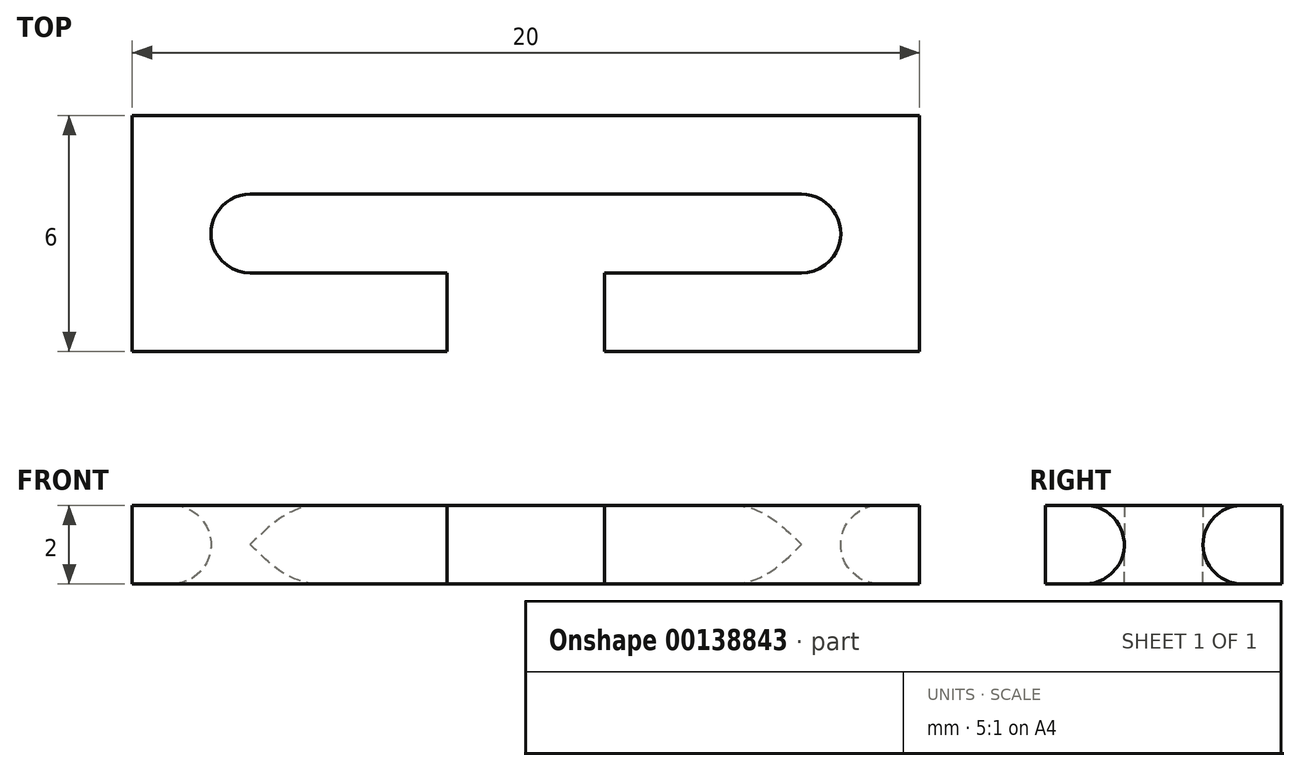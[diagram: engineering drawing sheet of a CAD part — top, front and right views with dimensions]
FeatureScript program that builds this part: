
annotation { "Feature Type Name" : "Feature", "Feature Type Description" : "" }
export const myFeature = defineFeature(function(context is Context, id is Id, definition is map)
    precondition{}
    {
        {
            var Q0;
            Q0=qCreatedBy(makeId("Top.planeOp"),FACE);
            var sketch = newSketch(context, id + "F0", { "sketchPlane" : qUnion([Q0])});
            skLineSegment(sketch, "E0.bottom", {"start": v(-2.27, -2.19) * mm, "end": v(17.73, -2.19) * mm});
            skLineSegment(sketch, "E0.top", {"start": v(-2.27, 3.81) * mm, "end": v(17.73, 3.81) * mm});
            skLineSegment(sketch, "E0.left", {"start": v(-2.27, -2.19) * mm, "end": v(-2.27, 3.81) * mm});
            skLineSegment(sketch, "E0.right", {"start": v(17.73, -2.19) * mm, "end": v(17.73, 3.81) * mm});
            skSolve(sketch);
        }
        {
            var Q0;
            Q0=makeQuery(id+"F0.imprint","IMPRINT",FACE,{"disambiguationData":[TD([[makeQuery(id+"F0.imprint","IMPRINT",EDGE,{"derivedFrom":sQuery(id+"F0.wireOp",EDGE,"E0.bottom")}),1.0]])]});
            extrude(context, id + "F1", {"entities" : qUnion([Q0]), "depth" : 2 * mm});
        }
        {
            var Q0;
            Q0=makeQuery(id+"F1.opExtrude","CAP_FACE",FACE,{"disambiguationData":[OSD([sQuery(id+"F0.wireOp",EDGE,"E0.bottom"),sQuery(id+"F0.wireOp",EDGE,"E0.top"),sQuery(id+"F0.wireOp",EDGE,"E0.left"),sQuery(id+"F0.wireOp",EDGE,"E0.right")])],"isStart":false});
            var Q1;
            Q1=makeQuery(id+"F1.opExtrude","CAP_FACE",FACE,{"disambiguationData":[OSD([sQuery(id+"F0.wireOp",EDGE,"E0.bottom"),sQuery(id+"F0.wireOp",EDGE,"E0.top"),sQuery(id+"F0.wireOp",EDGE,"E0.left"),sQuery(id+"F0.wireOp",EDGE,"E0.right")])],"isStart":true});
            shell(context, id + "F2", {"entities" : qUnion([Q0, Q1]), "thickness" : 2 * mm});
        }
        {
            var Q0;
            Q0=makeQuery(id+"F1.opExtrude","CAP_FACE",FACE,{"disambiguationData":[OSD([sQuery(id+"F0.wireOp",EDGE,"E0.bottom"),sQuery(id+"F0.wireOp",EDGE,"E0.top"),sQuery(id+"F0.wireOp",EDGE,"E0.left"),sQuery(id+"F0.wireOp",EDGE,"E0.right")])],"isStart":false});
            var sketch = newSketch(context, id + "F3", { "sketchPlane" : qUnion([Q0])});
            skLineSegment(sketch, "E1.bottom", {"start": v(5.73, -0.19) * mm, "end": v(9.73, -0.19) * mm});
            skLineSegment(sketch, "E1.top", {"start": v(5.73, -2.19) * mm, "end": v(9.73, -2.19) * mm});
            skLineSegment(sketch, "E1.left", {"start": v(5.73, -0.19) * mm, "end": v(5.73, -2.19) * mm});
            skLineSegment(sketch, "E1.right", {"start": v(9.73, -0.19) * mm, "end": v(9.73, -2.19) * mm});
            skSolve(sketch);
        }
        {
            var Q0;
            Q0=makeQuery(id+"F3.imprint","IMPRINT",FACE,{"disambiguationData":[TD([[makeQuery(id+"F3.imprint","IMPRINT",EDGE,{"derivedFrom":sQuery(id+"F3.wireOp",EDGE,"E1.bottom")}),-1.0]])]});
            extrude(context, id + "F4", {"entities" : qUnion([Q0]), "operationType" : NewBodyOperationType.REMOVE, "oppositeDirection" : true, "depth" : 25 * mm});
        }
        {
            var Q0;
            Q0=makeQuery(id+"F2.opShell","OFFSET_FACE",FACE,{"disambiguationData":[OSD([sQuery(id+"F0.wireOp",EDGE,"E0.left")])]});
            var Q1;
            Q1=makeQuery(id+"F2.opShell","OFFSET_FACE",FACE,{"disambiguationData":[OSD([sQuery(id+"F0.wireOp",EDGE,"E0.right")])]});
            fillet(context, id + "F5", {"entities" : qUnion([Q0, Q1]), "radius" : 1 * mm, "tangentPropagation" : true, "allowEdgeOverflow" : false});
        }
    });
